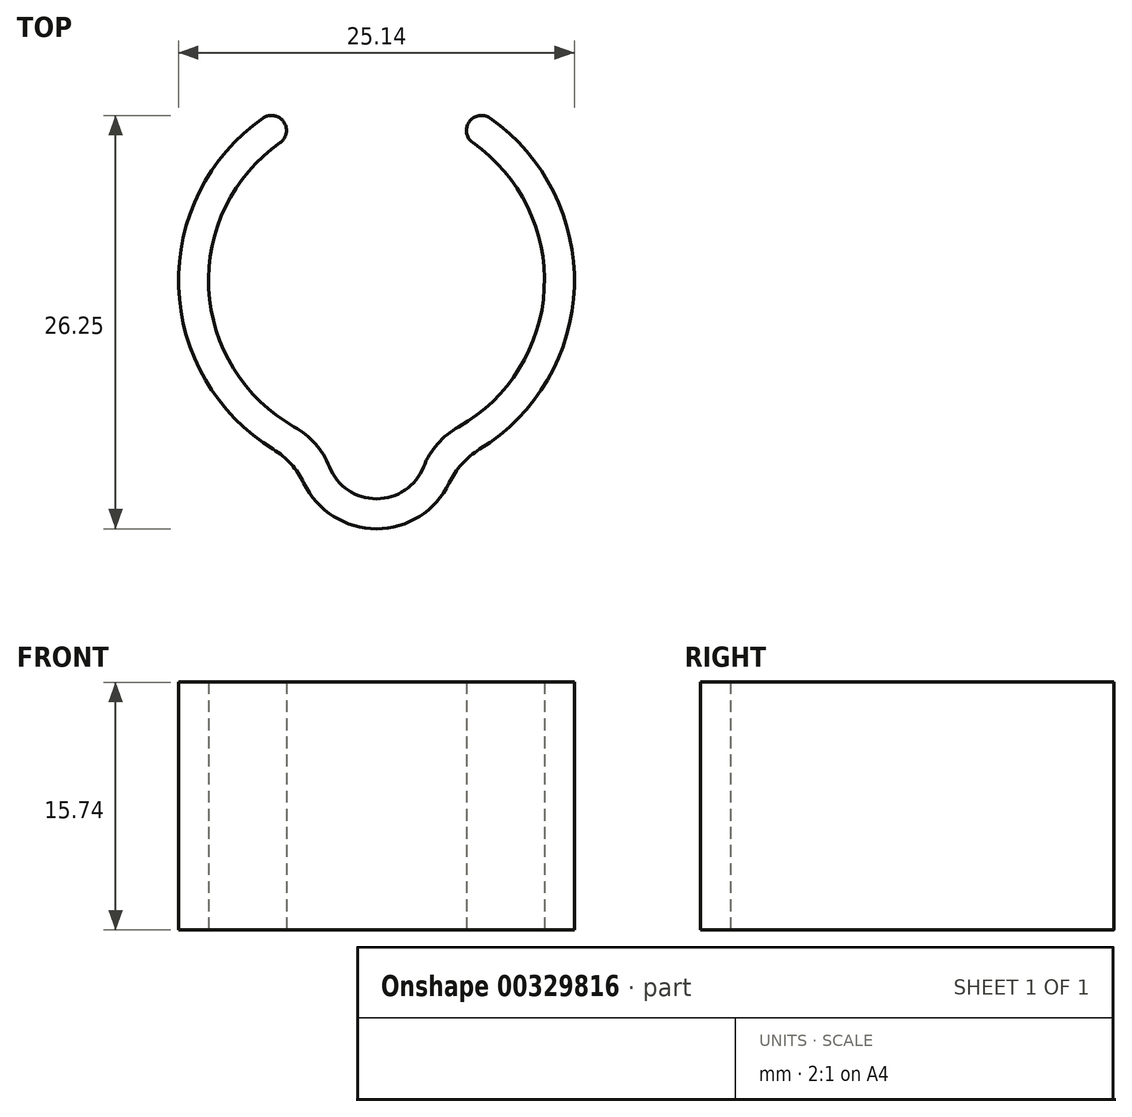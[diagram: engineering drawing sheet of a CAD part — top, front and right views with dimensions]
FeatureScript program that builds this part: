
annotation { "Feature Type Name" : "Feature", "Feature Type Description" : "" }
export const myFeature = defineFeature(function(context is Context, id is Id, definition is map)
    precondition{}
    {
        {
            var Q0;
            Q0=qCreatedBy(makeId("Top.planeOp"),FACE);
            var sketch = newSketch(context, id + "F0", { "sketchPlane" : qUnion([Q0])});
            skArc(sketch, "E0", {"start": v(-6.12, 8.74) * mm, "mid": v(-10.54, -1.64) * mm, "end": v(-3.18, -10.18) * mm});
            skArc(sketch, "E1", {"start": v(-7.21, 10.3) * mm, "mid": v(-12.51, -1.24) * mm, "end": v(-5.05, -11.52) * mm});
            skArc(sketch, "E2", {"start": v(-6.12, 8.74) * mm, "mid": v(-5.89, 10.06) * mm, "end": v(-7.21, 10.3) * mm});
            skArc(sketch, "E3", {"start": v(7.21, 10.3) * mm, "mid": v(5.89, 10.06) * mm, "end": v(6.12, 8.74) * mm});
            skArc(sketch, "E4.trimOffspring", {"start": v(5.05, -11.52) * mm, "mid": v(12.51, -1.24) * mm, "end": v(7.21, 10.3) * mm});
            skLineSegment(sketch, "E5", {"start": v(0, -10.67) * mm, "end": v(0, -15.78) * mm, "construction": true});
            skArc(sketch, "E6", {"start": v(-5.05, -11.52) * mm, "mid": v(0, -15.78) * mm, "end": v(5.05, -11.52) * mm});
            skArc(sketch, "E7", {"start": v(3.17, -10.18) * mm, "mid": v(10.54, -1.64) * mm, "end": v(6.12, 8.74) * mm});
            skArc(sketch, "E8", {"start": v(-3.18, -10.18) * mm, "mid": v(0, -13.88) * mm, "end": v(3.18, -10.18) * mm});
            skSolve(sketch);
        }
        {
            var Q0;
            Q0=qSketchRegion(id+"F0",true);
            var Q1;
            Q1=makeQuery(id+"F0.imprint","IMPRINT",FACE,{"disambiguationData":[TD([[makeQuery(id+"F0.imprint","IMPRINT",EDGE,{"derivedFrom":sQuery(id+"F0.wireOp",EDGE,"sMBprik8-b5Ds-yZTN-arfg-6G3kgr7FVDsM")}),1.0]])]});
            extrude(context, id + "F1", {"entities" : qUnion([Q0, Q1]), "endBound" : BoundingType.SYMMETRIC, "depth" : 15.75 * mm});
        }
        {
            var Q0;
            Q0=makeQuery(id+"F1.opExtrude","SWEPT_EDGE",EDGE,{"disambiguationData":[OSD([sQuery(id+"F0.wireOp",EDGE,"E1"),sQuery(id+"F0.wireOp",EDGE,"E6")])]});
            var Q1;
            Q1=makeQuery(id+"F1.opExtrude","SWEPT_EDGE",EDGE,{"disambiguationData":[OSD([sQuery(id+"F0.wireOp",EDGE,"E0"),sQuery(id+"F0.wireOp",EDGE,"E8")])]});
            var Q2;
            Q2=makeQuery(id+"F1.opExtrude","SWEPT_EDGE",EDGE,{"disambiguationData":[OSD([sQuery(id+"F0.wireOp",EDGE,"E7"),sQuery(id+"F0.wireOp",EDGE,"E8")])]});
            var Q3;
            Q3=makeQuery(id+"F1.opExtrude","SWEPT_EDGE",EDGE,{"disambiguationData":[OSD([sQuery(id+"F0.wireOp",EDGE,"E4.trimOffspring"),sQuery(id+"F0.wireOp",EDGE,"E6")])]});
            fillet(context, id + "F2", {"entities" : qUnion([Q0, Q1, Q2, Q3]), "radius" : 5.08 * mm, "tangentPropagation" : true, "allowEdgeOverflow" : false});
        }
    });
